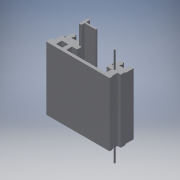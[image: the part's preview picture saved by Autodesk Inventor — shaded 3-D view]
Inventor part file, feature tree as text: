
AUTODESK INVENTOR PART (.ipt)
format: ipt  version: 2016 (Build 200138000, 138)  size: 321,024 bytes
history: native  units: mm
features: extrude x11, sketch x10, plane x1
ambient origin geometry x8: Origin, YZ Plane, XZ Plane, XY Plane, X Axis, Y Axis, Z Axis, Center Point
bodies: Solid1 (feature_tree)
feature tree (22):
  extrude  "Extrusion1"  Depth=199.0mm
  extrude  "Extrusion2"  Depth=2.0mm
  extrude  "Extrusion3"  Depth=18.0mm TaperAngle=0.0deg
  plane  "Work Plane1"
  sketch  "Sketch5"  dims[d9=10.0mm d10=14.0mm]
  extrude  "Extrusion4"  Depth=14.0mm
  extrude  "Extrusion5"  Depth=20.0mm
  sketch  "Sketch8"  dims[d13=2.0mm d14=199.0mm d15=0.0mm]
  extrude  "Extrusion6"  Depth=199.0mm TaperAngle=0.0deg
  extrude  "Extrusion7"  Depth=27.0mm
  sketch  "Sketch10"  dims[d18=1.5mm d19=1.5mm d20=11.05mm]
  extrude  "Extrusion8"  Depth=11.05mm
  extrude  "Extrusion9"  Depth=20.0mm
  sketch  "Sketch11"  dims[d21=193.0mm d22=0.0mm d29=20.0mm]
  extrude  "Extrusion10"  Depth=27.0mm
  extrude  "Extrusion11"  Depth=193.0mm TaperAngle=0.0deg
  sketch  "Sketch1"  dims[d0=199.0mm d1=199.0mm]
  sketch  "Sketch2"  dims[d2=9.0mm d3=0.0mm d4=2.0mm]
  sketch  "Sketch4"  dims[d5=19.0mm d6=18.0mm d7=0.0mm]
  sketch  "Sketch6"  dims[d11=15.0mm d12=20.0mm]
  sketch  "Sketch9"  dims[d16=-3.0mm d17=27.0mm]
  sketch  "Sketch12"  dims[d30=199.0mm d31=0.0mm d32=27.0mm d33=1.5mm d34=1.5mm d35=11.05mm d36=193.0mm d37=0.0mm d38=5.0mm d39=3.0mm d40=199.0mm d41=0.0mm d42=35.0mm d43=199.0mm d44=0.0mm d45=60.0mm d46=0.0mm d47=5.0mm d50=5.0mm d51=55.0mm d52=0.0mm d53=55.0mm d54=0.0mm d55=14.0mm d56=32.0mm d57=18.0mm d59=27.0mm d60=12.5mm d61=5.0mm]
